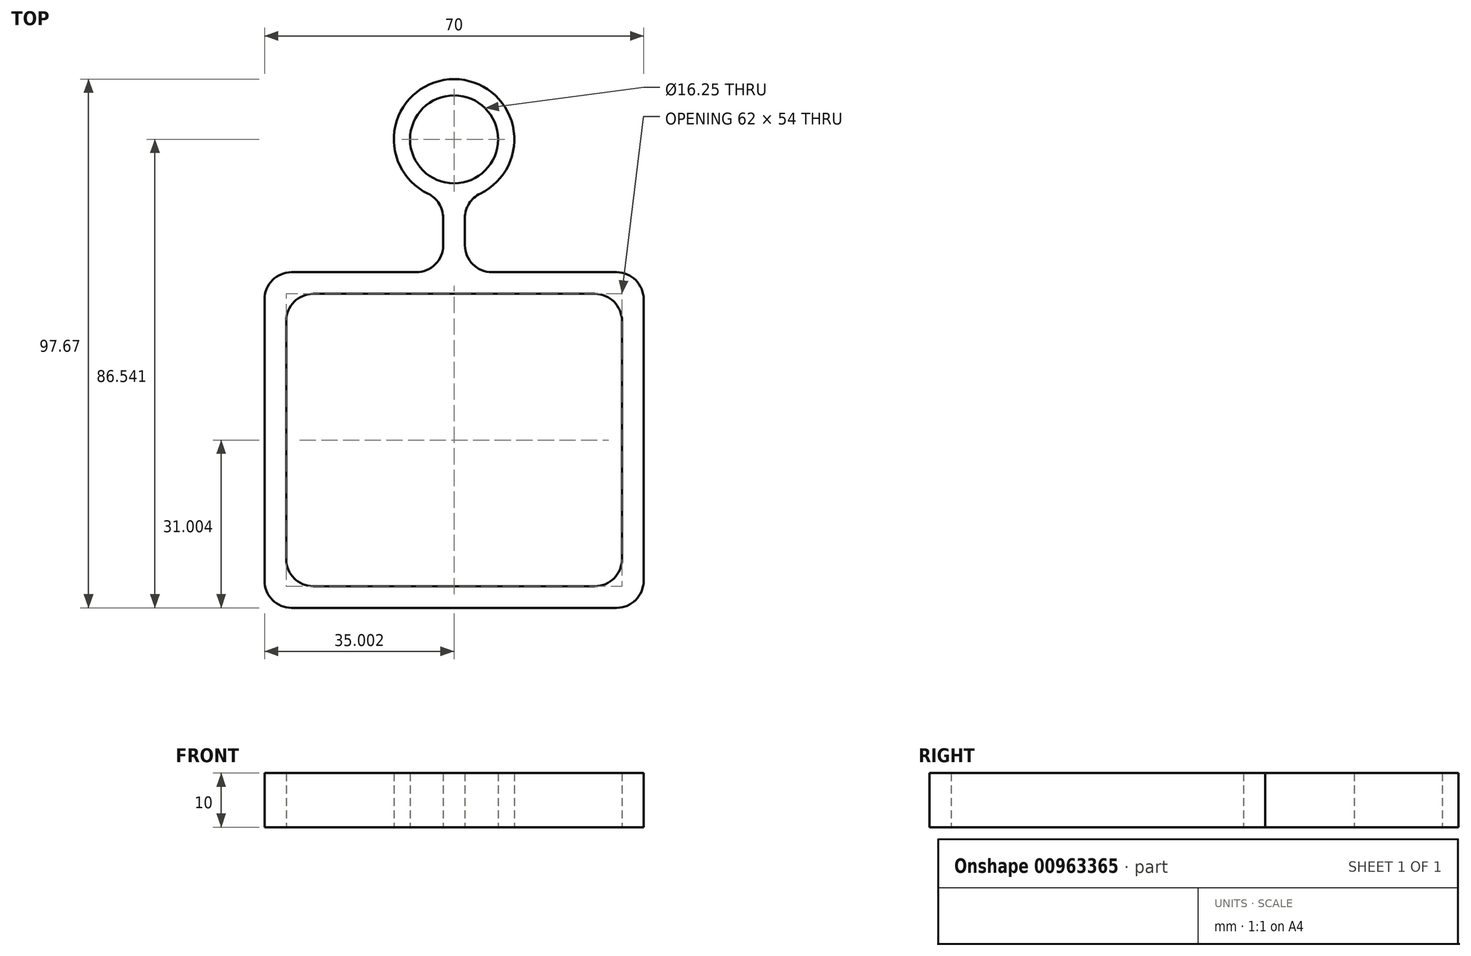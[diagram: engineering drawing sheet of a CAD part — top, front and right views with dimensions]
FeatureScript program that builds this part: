
annotation { "Feature Type Name" : "Feature", "Feature Type Description" : "" }
export const myFeature = defineFeature(function(context is Context, id is Id, definition is map)
    precondition{}
    {
        {
            var Q0;
            Q0=qCreatedBy(makeId("Top.planeOp"),FACE);
            var sketch = newSketch(context, id + "F0", { "sketchPlane" : qUnion([Q0])});
            skLineSegment(sketch, "E0.bottom", {"start": v(-32.1, 37) * mm, "end": v(19.9, 37) * mm});
            skLineSegment(sketch, "E0.top", {"start": v(-32.1, -17) * mm, "end": v(19.9, -17) * mm});
            skLineSegment(sketch, "E0.left", {"start": v(-37.1, 32) * mm, "end": v(-37.1, -12) * mm});
            skLineSegment(sketch, "E0.right", {"start": v(24.9, 32) * mm, "end": v(24.9, -12) * mm});
            skLineSegment(sketch, "E1.0", {"start": v(-36.1, 41) * mm, "end": v(-8.1, 41) * mm});
            skLineSegment(sketch, "E1.1", {"start": v(-41.1, 36) * mm, "end": v(-41.1, -16) * mm});
            skLineSegment(sketch, "E1.2", {"start": v(-36.1, -21) * mm, "end": v(23.9, -21) * mm});
            skLineSegment(sketch, "E1.3", {"start": v(28.9, 36) * mm, "end": v(28.9, -16) * mm});
            skLineSegment(sketch, "E2.left", {"start": v(-8.1, 41) * mm, "end": v(-8.1, 54.59) * mm});
            skLineSegment(sketch, "E2.right", {"start": v(-4.1, 41) * mm, "end": v(-4.1, 54.59) * mm});
            skPoint(sketch, "E2.middle", {"position": v(-6.1, 53.26) * mm});
            skLineSegment(sketch, "E3", {"start": v(-6.1, 53.26) * mm, "end": v(-6.1, 54.4) * mm, "construction": true});
            skCircle(sketch, "E4", {"center": v(-6.1, 65.53) * mm, "radius": 8.12 * mm});
            skCircle(sketch, "E5.0", {"center": v(-6.1, 65.53) * mm, "radius": 11.12 * mm});
            skPoint(sketch, "E6.visualSharp", {"position": v(-37.1, 37) * mm});
            skArc(sketch, "E6.filletArc", {"start": v(-32.1, 37) * mm, "mid": v(-35.64, 35.53) * mm, "end": v(-37.1, 32) * mm});
            skPoint(sketch, "E7.visualSharp", {"position": v(24.9, 37) * mm});
            skArc(sketch, "E7.filletArc", {"start": v(24.9, 32) * mm, "mid": v(23.43, 35.53) * mm, "end": v(19.9, 37) * mm});
            skPoint(sketch, "E8.visualSharp", {"position": v(24.9, -17) * mm});
            skArc(sketch, "E8.filletArc", {"start": v(19.9, -17) * mm, "mid": v(23.43, -15.54) * mm, "end": v(24.9, -12) * mm});
            skPoint(sketch, "E9.visualSharp", {"position": v(-37.1, -17) * mm});
            skArc(sketch, "E9.filletArc", {"start": v(-37.1, -12) * mm, "mid": v(-35.64, -15.54) * mm, "end": v(-32.1, -17) * mm});
            skPoint(sketch, "E10.visualSharp", {"position": v(-41.1, 41) * mm});
            skArc(sketch, "E10.filletArc", {"start": v(-36.1, 41) * mm, "mid": v(-39.64, 39.53) * mm, "end": v(-41.1, 36) * mm});
            skPoint(sketch, "E11.visualSharp", {"position": v(28.9, 41) * mm});
            skArc(sketch, "E11.filletArc", {"start": v(28.9, 36) * mm, "mid": v(27.43, 39.53) * mm, "end": v(23.9, 41) * mm});
            skPoint(sketch, "E12.visualSharp", {"position": v(28.9, -21) * mm});
            skArc(sketch, "E12.filletArc", {"start": v(23.9, -21) * mm, "mid": v(27.43, -19.54) * mm, "end": v(28.9, -16) * mm});
            skPoint(sketch, "E13.visualSharp", {"position": v(-41.1, -21) * mm});
            skArc(sketch, "E13.filletArc", {"start": v(-41.1, -16) * mm, "mid": v(-39.64, -19.54) * mm, "end": v(-36.1, -21) * mm});
            skPoint(sketch, "E14.orphan", {"position": v(-4.1, 65.53) * mm});
            skPoint(sketch, "E2.top.start.orphan", {"position": v(-8.1, 65.53) * mm});
            skPoint(sketch, "E15.start.orphan", {"position": v(-6.1, 41) * mm});
            skLineSegment(sketch, "E16.trimOffspring", {"start": v(-4.1, 41) * mm, "end": v(23.9, 41) * mm});
            skSolve(sketch);
        }
        {
            var Q0;
            Q0=makeQuery(id+"F0.imprint","IMPRINT",FACE,{"disambiguationData":[TD([[makeQuery(id+"F0.imprint","IMPRINT",EDGE,{"derivedFrom":sQuery(id+"F0.wireOp",EDGE,"E4")}),-1.0]])]});
            var Q1;
            Q1=makeQuery(id+"F0.imprint","IMPRINT",FACE,{"disambiguationData":[TD([[makeQuery(id+"F0.imprint","IMPRINT",EDGE,{"derivedFrom":sQuery(id+"F0.wireOp",EDGE,"E0.bottom")}),1.0]])]});
            extrude(context, id + "F1", {"entities" : qUnion([Q0, Q1]), "depth" : 10 * mm, "offsetDistance" : 25 * mm});
        }
        {
            var Q0;
            Q0=makeQuery(id+"F1.opExtrude","SWEPT_EDGE",EDGE,{"disambiguationData":[OSD([sQuery(id+"F0.wireOp",EDGE,"E2.right"),sQuery(id+"F0.wireOp",EDGE,"E5.0")])]});
            var Q1;
            Q1=makeQuery(id+"F1.opExtrude","SWEPT_EDGE",EDGE,{"disambiguationData":[OSD([sQuery(id+"F0.wireOp",EDGE,"E2.left"),sQuery(id+"F0.wireOp",EDGE,"E5.0")])]});
            var Q2;
            Q2=makeQuery(id+"F1.opExtrude","SWEPT_EDGE",EDGE,{"disambiguationData":[OSD([sQuery(id+"F0.wireOp",EDGE,"E1.0"),sQuery(id+"F0.wireOp",EDGE,"E2.left")])]});
            var Q3;
            Q3=makeQuery(id+"F1.opExtrude","SWEPT_EDGE",EDGE,{"disambiguationData":[OSD([sQuery(id+"F0.wireOp",EDGE,"E2.right"),sQuery(id+"F0.wireOp",EDGE,"E16.trimOffspring")])]});
            fillet(context, id + "F2", {"entities" : qUnion([Q0, Q1, Q2, Q3]), "radius" : 5 * mm, "tangentPropagation" : true, "allowEdgeOverflow" : false});
        }
    });
